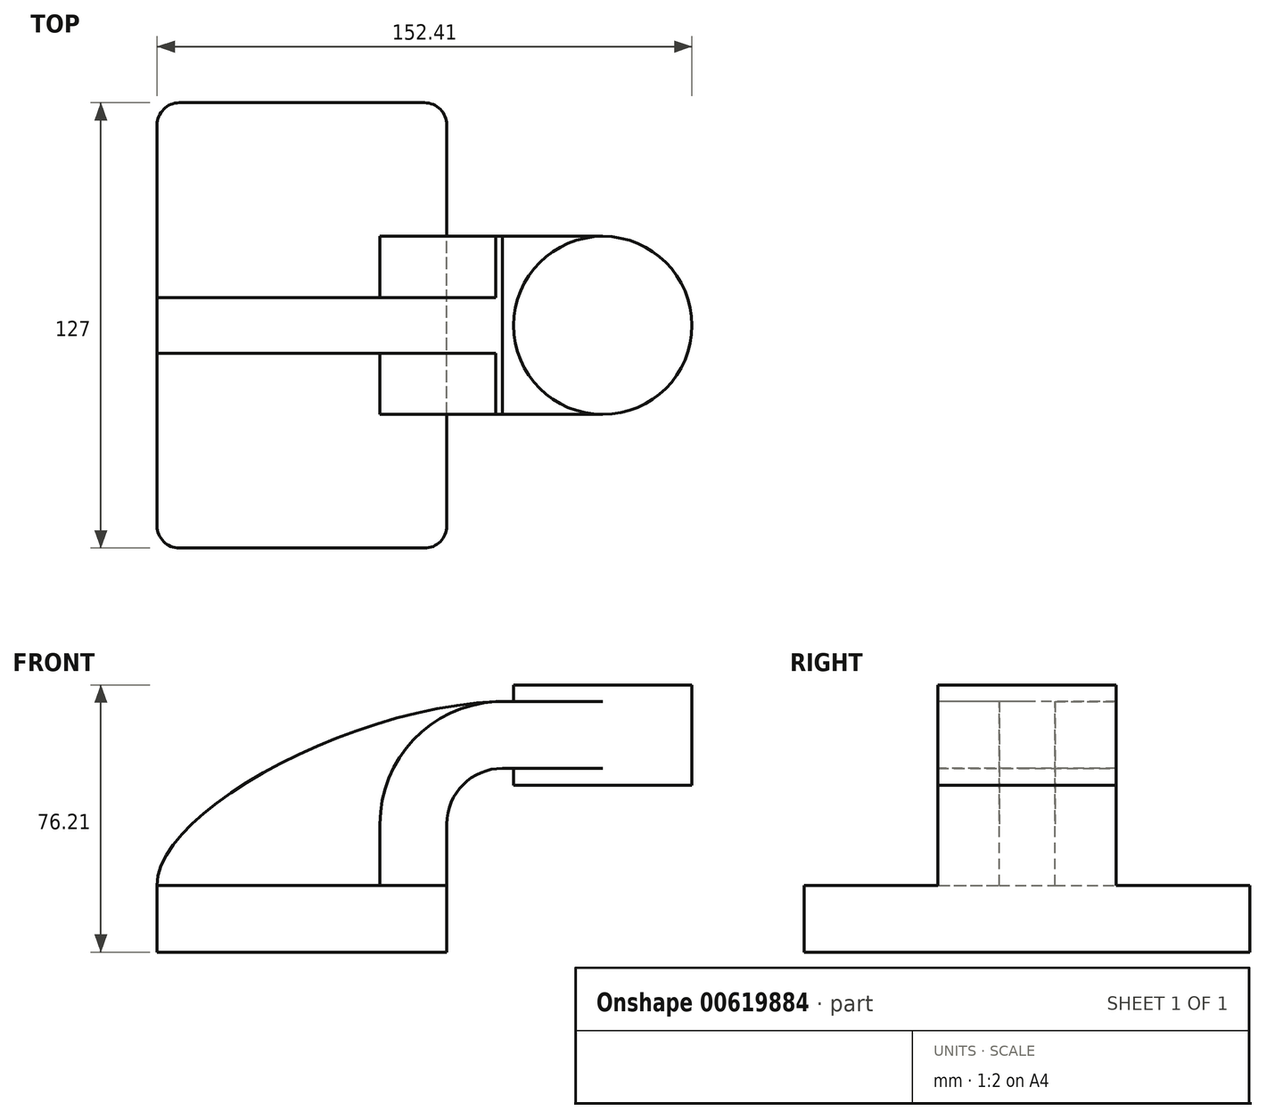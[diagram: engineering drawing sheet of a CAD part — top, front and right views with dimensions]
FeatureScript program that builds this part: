
annotation { "Feature Type Name" : "Feature", "Feature Type Description" : "" }
export const myFeature = defineFeature(function(context is Context, id is Id, definition is map)
    precondition{}
    {
        {
            var Q0;
            Q0=qCreatedBy(makeId("Front.planeOp"),FACE);
            var sketch = newSketch(context, id + "F0", { "sketchPlane" : qUnion([Q0])});
            skPoint(sketch, "E0.middle", {"position": v(0, 0) * mm});
            skLineSegment(sketch, "E1.bottom", {"start": v(111.12, 38.1) * mm, "end": v(60.33, 38.1) * mm});
            skLineSegment(sketch, "E1.top", {"start": v(111.12, 66.68) * mm, "end": v(60.33, 66.68) * mm});
            skLineSegment(sketch, "E1.left", {"start": v(111.12, 38.1) * mm, "end": v(111.12, 66.68) * mm});
            skLineSegment(sketch, "E1.right", {"start": v(60.33, 38.1) * mm, "end": v(60.33, 66.68) * mm});
            skPoint(sketch, "E1.middle", {"position": v(85.72, 52.39) * mm});
            skLineSegment(sketch, "E2.bottom", {"start": v(41.28, -9.52) * mm, "end": v(-41.28, -9.52) * mm});
            skLineSegment(sketch, "E2.top", {"start": v(41.28, 9.53) * mm, "end": v(-41.28, 9.53) * mm});
            skLineSegment(sketch, "E2.left", {"start": v(41.28, -9.52) * mm, "end": v(41.28, 9.53) * mm});
            skLineSegment(sketch, "E2.right", {"start": v(-41.28, -9.52) * mm, "end": v(-41.28, 9.53) * mm});
            skLineSegment(sketch, "E3", {"start": v(41.28, 9.53) * mm, "end": v(41.28, 27) * mm});
            skArc(sketch, "E4", {"start": v(41.27, 27) * mm, "mid": v(45.92, 38.23) * mm, "end": v(57.15, 42.88) * mm});
            skLineSegment(sketch, "E5", {"start": v(57.15, 42.88) * mm, "end": v(85.72, 42.88) * mm});
            skLineSegment(sketch, "E6.0", {"start": v(57.15, 61.93) * mm, "end": v(85.72, 61.93) * mm});
            skArc(sketch, "E6.1", {"start": v(22.23, 27) * mm, "mid": v(32.45, 51.7) * mm, "end": v(57.15, 61.93) * mm});
            skLineSegment(sketch, "E6.2", {"start": v(22.22, 9.53) * mm, "end": v(22.22, 27) * mm});
            skLineSegment(sketch, "E7", {"start": v(85.72, 38.1) * mm, "end": v(85.72, 66.68) * mm});
            skFitSpline(sketch, "E8", {"points": [v(-41.28, 9.52) * mm, v(57.15, 61.93) * mm], "startDerivative": vector(-0.75, 63.8) * mm, "endDerivative": vector(124.3, 2.17) * mm});
            skSolve(sketch);
        }
        {
            var Q0;
            Q0=makeQuery(id+"F0.imprint","IMPRINT",FACE,{"disambiguationData":[TD([[makeQuery(id+"F0.imprint","IMPRINT",EDGE,{"derivedFrom":sQuery(id+"F0.wireOp",EDGE,"E2.bottom")}),-1.0]])]});
            extrude(context, id + "F1", {"entities" : qUnion([Q0]), "endBound" : BoundingType.SYMMETRIC, "depth" : 127 * mm, "offsetDistance" : 25.4 * mm});
        }
        {
            var Q0;
            {var subQ0=sQuery(id+"F0.wireOp",EDGE,"E3");Q0=makeQuery(id+"F0.imprint","IMPRINT",FACE,{"disambiguationData":[TD([[makeQuery(id+"F0.imprint","IMPRINT",EDGE,{"derivedFrom":subQ0}),1.0]])]});}
            var Q1;
            {var subQ0=sQuery(id+"F0.wireOp",EDGE,"E5");var subQ1=sQuery(id+"F0.wireOp",EDGE,"E1.right");var subQ2=makeQuery(id+"F0.imprint","INTERSECT",VERTEX,{"derivedFrom":[subQ1,subQ0]});Q1=makeQuery(id+"F0.imprint","IMPRINT",FACE,{"disambiguationData":[TD([[makeQuery(id+"F0.imprint","IMPRINT",EDGE,{"disambiguationData":[TD([[subQ2,-1.0]])],"derivedFrom":subQ1}),-1.0]])]});}
            extrude(context, id + "F2", {"entities" : qUnion([Q0, Q1]), "operationType" : NewBodyOperationType.ADD, "endBound" : BoundingType.SYMMETRIC, "depth" : 50.8 * mm, "offsetDistance" : 25.4 * mm});
        }
        {
            var Q0;
            {var subQ3=sQuery(id+"F0.wireOp",EDGE,"E6.2");Q0=makeQuery(id+"F0.imprint","IMPRINT",FACE,{"disambiguationData":[TD([[makeQuery(id+"F0.imprint","IMPRINT",EDGE,{"derivedFrom":subQ3}),1.0]])]});}
            extrude(context, id + "F3", {"entities" : qUnion([Q0]), "operationType" : NewBodyOperationType.ADD, "endBound" : BoundingType.SYMMETRIC, "depth" : 15.88 * mm, "offsetDistance" : 25.4 * mm});
        }
        {
            var Q0;
            {var subQ0=sQuery(id+"F0.wireOp",EDGE,"E1.left");Q0=makeQuery(id+"F0.imprint","IMPRINT",FACE,{"disambiguationData":[TD([[makeQuery(id+"F0.imprint","IMPRINT",EDGE,{"derivedFrom":subQ0}),1.0]])]});}
            var Q1;
            Q1=sQuery(id+"F0.wireOp",EDGE,"E7");
            revolve(context, id + "F4", {"operationType" : NewBodyOperationType.ADD, "entities" : qUnion([Q0]), "axis" : qUnion([Q1]), "revolveType" : RevolveType.FULL});
        }
        {
            var Q0;
            Q0=makeQuery(id+"F1.opExtrude","CAP_EDGE",EDGE,{"disambiguationData":[OSD([sQuery(id+"F0.wireOp",EDGE,"E2.left")])],"isStart":false});
            var Q1;
            Q1=makeQuery(id+"F1.opExtrude","CAP_EDGE",EDGE,{"disambiguationData":[OSD([sQuery(id+"F0.wireOp",EDGE,"E2.right")])],"isStart":false});
            var Q2;
            Q2=makeQuery(id+"F1.opExtrude","CAP_EDGE",EDGE,{"disambiguationData":[OSD([sQuery(id+"F0.wireOp",EDGE,"E2.left")])],"isStart":true});
            var Q3;
            Q3=makeQuery(id+"F1.opExtrude","CAP_EDGE",EDGE,{"disambiguationData":[OSD([sQuery(id+"F0.wireOp",EDGE,"E2.right")])],"isStart":true});
            fillet(context, id + "F5", {"entities" : qUnion([Q0, Q1, Q2, Q3]), "radius" : 6.35 * mm, "tangentPropagation" : true, "allowEdgeOverflow" : false});
        }
    });
